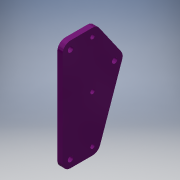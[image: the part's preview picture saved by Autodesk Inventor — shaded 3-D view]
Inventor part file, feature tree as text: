
AUTODESK INVENTOR PART (.ipt)
format: ipt  version: 2017 SP1 (Build 210196100, 196)  size: 129,536 bytes
history: native  units: in
note: dims shown in document units (in); Inventor stores cm internally (conversion verified against a paired STEP export)
features: extrude x1, sketch x1
ambient origin geometry x8: Origin, YZ Plane, XZ Plane, XY Plane, X Axis, Y Axis, Z Axis, Center Point
bodies: Solid1 (feature_tree)
feature tree (2):
  extrude  "Extrusion1"  Depth=0.25in
  sketch  "Sketch1"  dims[d0=1.0in d1=0.26in d2=0.548in d3=1.25in d4=1.5in d5=3.0in d6=0.375in d7=0.25in d8=0.0in d9=0.21in]
